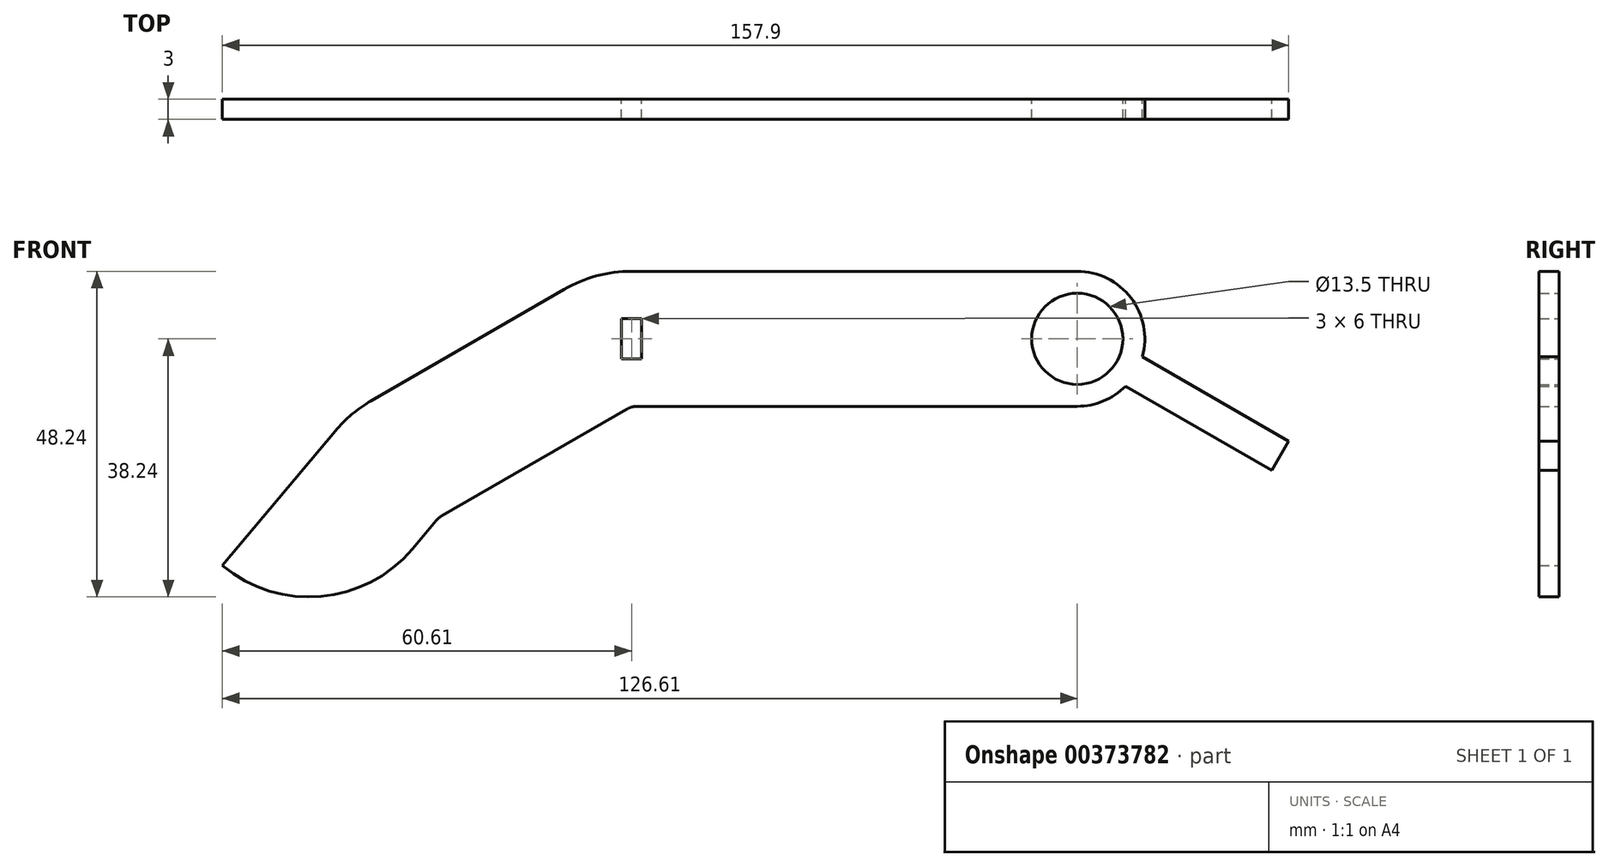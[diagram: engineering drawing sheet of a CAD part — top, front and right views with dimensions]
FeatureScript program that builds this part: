
annotation { "Feature Type Name" : "Feature", "Feature Type Description" : "" }
export const myFeature = defineFeature(function(context is Context, id is Id, definition is map)
    precondition{}
    {
        {
            var Q0;
            Q0=qCreatedBy(makeId("Front.planeOp"),FACE);
            var sketch = newSketch(context, id + "F0", { "sketchPlane" : qUnion([Q0])});
            skLineSegment(sketch, "E0.bottom", {"start": v(33, -10) * mm, "end": v(-33, -10) * mm});
            skLineSegment(sketch, "E0.top", {"start": v(33, 10) * mm, "end": v(-33, 10) * mm});
            skLineSegment(sketch, "E0.left", {"start": v(33, -10) * mm, "end": v(33, 10) * mm, "construction": true});
            skLineSegment(sketch, "E0.right", {"start": v(-33, -10) * mm, "end": v(-33, 10) * mm, "construction": true});
            skPoint(sketch, "E0.middle", {"position": v(0, 0) * mm});
            skArc(sketch, "E1", {"start": v(-33, 10) * mm, "mid": v(-38.18, 9.32) * mm, "end": v(-43, 7.32) * mm});
            skLineSegment(sketch, "E2", {"start": v(-43, 7.32) * mm, "end": v(-33, -10) * mm, "construction": true});
            skLineSegment(sketch, "E3", {"start": v(-43, 7.32) * mm, "end": v(-71.58, -9.18) * mm});
            skLineSegment(sketch, "E4", {"start": v(-33, -10) * mm, "end": v(-61.58, -26.5) * mm});
            skLineSegment(sketch, "E5", {"start": v(-71.58, -9.18) * mm, "end": v(-61.58, -26.5) * mm, "construction": true});
            skArc(sketch, "E6", {"start": v(-71.58, -9.18) * mm, "mid": v(-74.43, -11.18) * mm, "end": v(-76.9, -13.64) * mm});
            skLineSegment(sketch, "E7", {"start": v(-76.9, -13.64) * mm, "end": v(-61.58, -26.5) * mm, "construction": true});
            skLineSegment(sketch, "E8", {"start": v(-76.9, -13.64) * mm, "end": v(-93.61, -33.56) * mm});
            skLineSegment(sketch, "E9", {"start": v(-61.58, -26.5) * mm, "end": v(-65.44, -31.1) * mm});
            skArc(sketch, "E10", {"start": v(-93.61, -33.56) * mm, "mid": v(-79.01, -38.16) * mm, "end": v(-65.44, -31.1) * mm});
            skCircle(sketch, "E11", {"center": v(33, 0) * mm, "radius": 6.75 * mm});
            skLineSegment(sketch, "E12", {"start": v(33, 0) * mm, "end": v(63.04, -17.34) * mm, "construction": true});
            skArc(sketch, "E13", {"start": v(33, 10) * mm, "mid": v(40.96, 6.05) * mm, "end": v(42.64, -2.68) * mm});
            skArc(sketch, "E14", {"start": v(33, -10) * mm, "mid": v(36.87, -9.22) * mm, "end": v(40.14, -7) * mm});
            skLineSegment(sketch, "E15", {"start": v(40.14, -7) * mm, "end": v(61.79, -19.5) * mm});
            skLineSegment(sketch, "E16", {"start": v(61.79, -19.5) * mm, "end": v(64.29, -15.18) * mm});
            skLineSegment(sketch, "E17", {"start": v(64.29, -15.18) * mm, "end": v(42.64, -2.68) * mm});
            skLineSegment(sketch, "E18.bottom", {"start": v(-31.5, -3) * mm, "end": v(-34.5, -3) * mm});
            skLineSegment(sketch, "E18.top", {"start": v(-31.5, 3) * mm, "end": v(-34.5, 3) * mm});
            skLineSegment(sketch, "E18.left", {"start": v(-31.5, -3) * mm, "end": v(-31.5, 3) * mm});
            skLineSegment(sketch, "E18.right", {"start": v(-34.5, -3) * mm, "end": v(-34.5, 3) * mm});
            skPoint(sketch, "E18.middle", {"position": v(-33, 0) * mm});
            skSolve(sketch);
        }
        {
            var Q0;
            Q0=qSketchRegion(id+"F0",true);
            extrude(context, id + "F1", {"entities" : qUnion([Q0]), "depth" : 3 * mm});
        }
        {
            var Q0;
            Q0=makeQuery(id+"F1.opExtrude","SWEPT_EDGE",EDGE,{"disambiguationData":[OSD([sQuery(id+"F0.wireOp",EDGE,"E0.bottom"),sQuery(id+"F0.wireOp",EDGE,"E4")])]});
            var Q1;
            Q1=makeQuery(id+"F1.opExtrude","SWEPT_EDGE",EDGE,{"disambiguationData":[OSD([sQuery(id+"F0.wireOp",EDGE,"E4"),sQuery(id+"F0.wireOp",EDGE,"E9")])]});
            fillet(context, id + "F2", {"entities" : qUnion([Q0, Q1]), "radius" : 3 * mm, "tangentPropagation" : true, "allowEdgeOverflow" : false});
        }
    });
